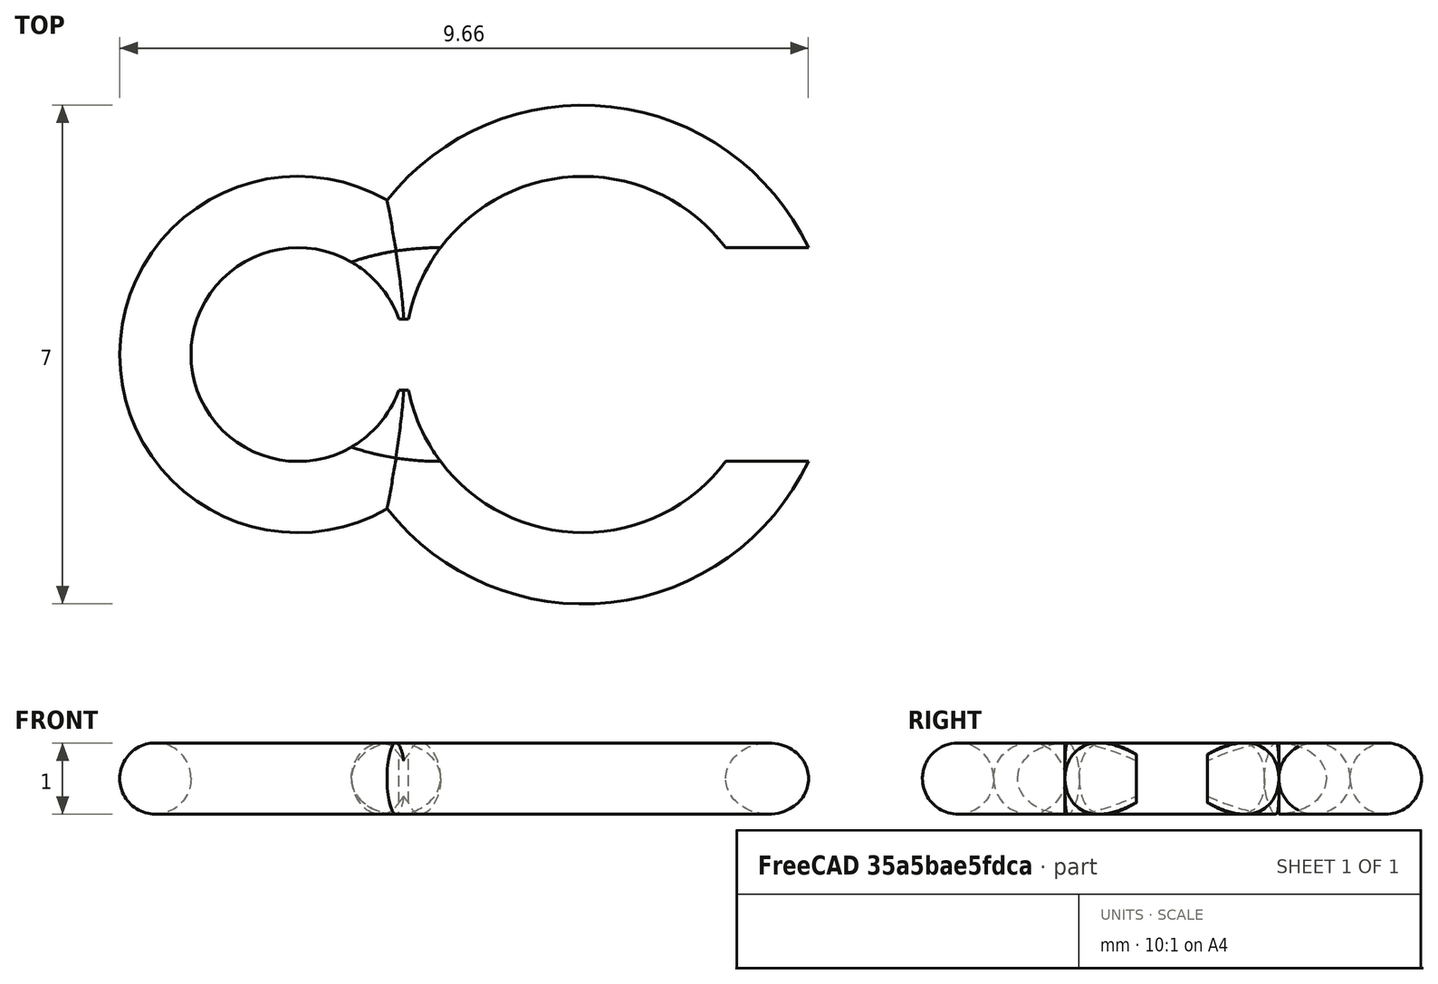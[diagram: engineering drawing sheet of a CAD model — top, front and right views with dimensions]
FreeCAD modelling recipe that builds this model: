
FCSTD DOCUMENT  (FreeCAD 0.16R)
Label: Auriculares Edu
License: All rights reserved
LicenseURL: http://en.wikipedia.org/wiki/All_rights_reserved
objects: Part::Cut×4, Part::Torus×2, Part::Cylinder×2, Part::Box×2, Part::MultiFuse×1
note: 11 computed .brp shape members not serialized (recipe doc carries the construction recipe); baked Part::Feature solids carry a one-line shape summary decoded from their .brp

FEATURE [Part::Torus] Torus  label="Toro"
  Angle1 = -180
  Angle2 = 180
  Angle3 = 360
  Placement = pos=(-1,0,0) rot=(0,0,1;0rad)
  Radius1 = 3
  Radius2 = 0.5
FEATURE [Part::Torus] Torus001  label="Toro001"
  Angle1 = -180
  Angle2 = 180
  Angle3 = 360
  Placement = pos=(-5,0,0) rot=(0,0,1;0rad)
  Radius1 = 2
  Radius2 = 0.5
FEATURE [Part::MultiFuse] Fusion
  Shapes = -> [Torus001,Torus]
FEATURE [Part::Cylinder] Cylinder  label="Cilindro"
  Angle = 360
  Height = 10
  Placement = pos=(-5,0,-4) rot=(0,0,1;0rad)
  Radius = 1.5
FEATURE [Part::Cut] Cut
  Base = -> Fusion
  Tool = -> Cylinder
FEATURE [Part::Cylinder] Cylinder001  label="Cilindro001"
  Angle = 360
  Height = 10
  Placement = pos=(-1,0,-9) rot=(0,0,1;0rad)
  Radius = 2.5
FEATURE [Part::Cut] Cut001
  Base = -> Cut
  Tool = -> Cylinder001
FEATURE [Part::Box] Box  label="Cubo"
  Height = 5
  Length = 3
  Placement = pos=(-4,-0.5,-3) rot=(0,0,1;0rad)
  Width = 1
FEATURE [Part::Cut] Cut002
  Base = -> Cut001
  Tool = -> Box
FEATURE [Part::Box] Box001  label="Cubo001"
  Height = 10
  Length = 4
  Placement = pos=(0,-1.5,-6) rot=(0,0,1;0rad)
  Width = 3
FEATURE [Part::Cut] Cut003
  Base = -> Cut002
  Tool = -> Box001
